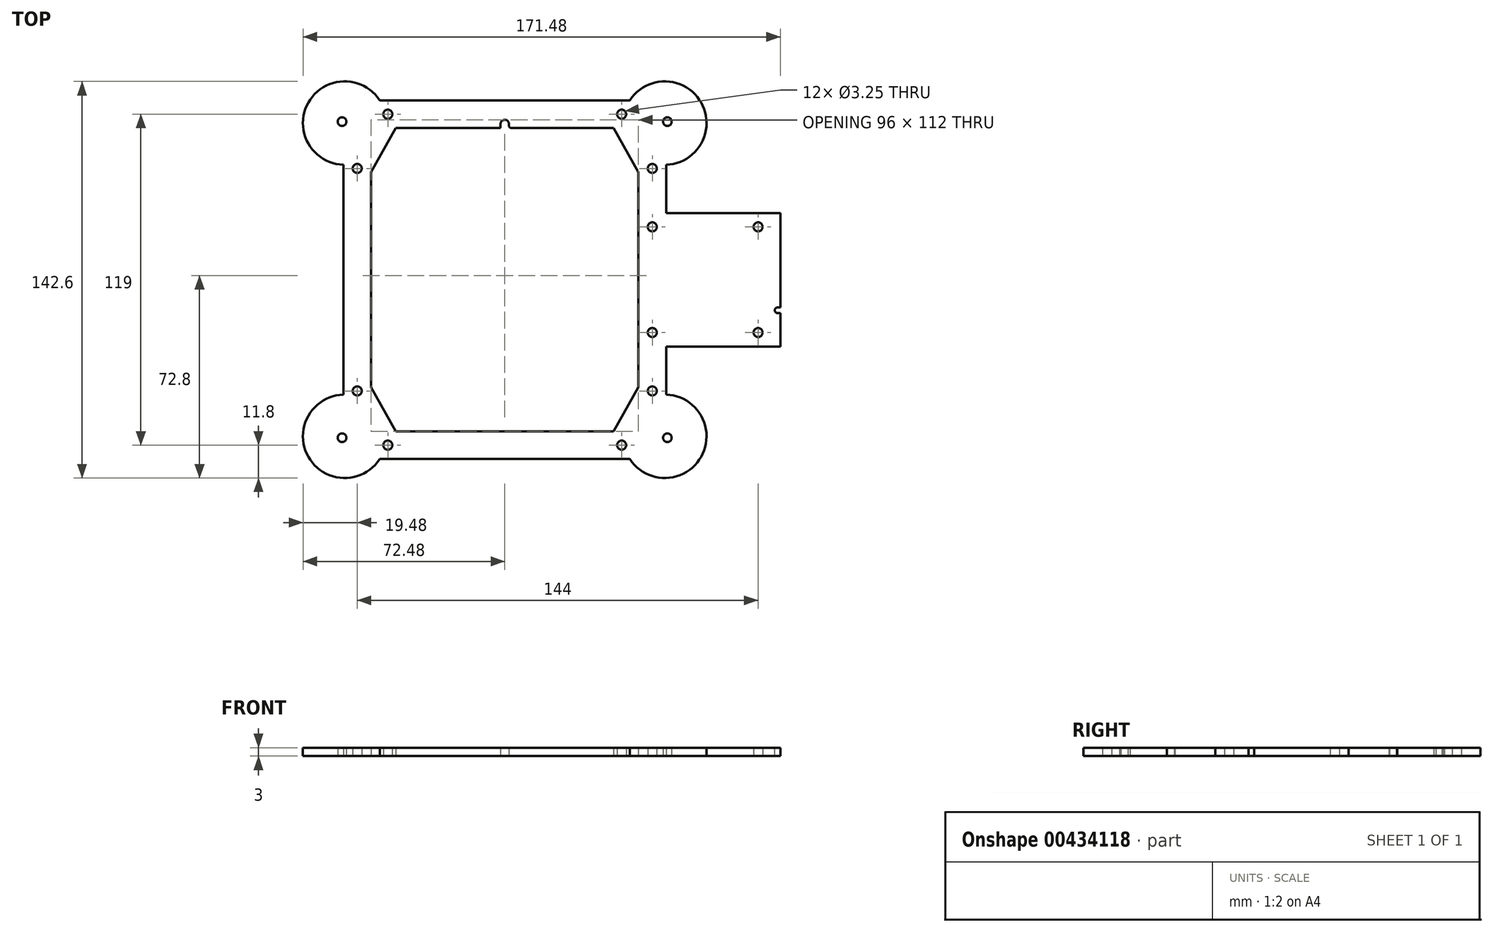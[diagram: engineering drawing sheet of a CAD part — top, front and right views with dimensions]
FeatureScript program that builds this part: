
annotation { "Feature Type Name" : "Feature", "Feature Type Description" : "" }
export const myFeature = defineFeature(function(context is Context, id is Id, definition is map)
    precondition{}
    {
        {
            var Q0;
            Q0=qCreatedBy(makeId("Top.planeOp"),FACE);
            var sketch = newSketch(context, id + "F0", { "sketchPlane" : qUnion([Q0])});
            skLineSegment(sketch, "E0", {"start": v(0, 0) * mm, "end": v(74.97, 0) * mm, "construction": true});
            skLineSegment(sketch, "E1", {"start": v(0, 0) * mm, "end": v(0, 75.03) * mm, "construction": true});
            skCircle(sketch, "E2", {"center": v(53, 40) * mm, "radius": 1.63 * mm});
            skCircle(sketch, "E3.MirrorC", {"center": v(-53, 40) * mm, "radius": 1.63 * mm});
            skCircle(sketch, "E4.MirrorC", {"center": v(-53, -40) * mm, "radius": 1.63 * mm});
            skCircle(sketch, "E5.MirrorC", {"center": v(53, -40) * mm, "radius": 1.63 * mm});
            skCircle(sketch, "E6", {"center": v(42, 59.5) * mm, "radius": 1.63 * mm});
            skCircle(sketch, "E7.MirrorC", {"center": v(-42, 59.5) * mm, "radius": 1.63 * mm});
            skCircle(sketch, "E8.MirrorC", {"center": v(-42, -59.5) * mm, "radius": 1.63 * mm});
            skCircle(sketch, "E9.MirrorC", {"center": v(42, -59.5) * mm, "radius": 1.63 * mm});
            skLineSegment(sketch, "E10", {"start": v(0, 59.5) * mm, "end": v(42, 59.5) * mm, "construction": true});
            skLineSegment(sketch, "E11", {"start": v(42, 59.5) * mm, "end": v(53, 40) * mm, "construction": true});
            skLineSegment(sketch, "E12", {"start": v(53, 40) * mm, "end": v(53, 0) * mm, "construction": true});
            skLineSegment(sketch, "E13.0", {"start": v(48, 38.69) * mm, "end": v(48, 0) * mm});
            skLineSegment(sketch, "E13.1", {"start": v(39.08, 54.5) * mm, "end": v(48, 38.69) * mm});
            skLineSegment(sketch, "E13.2", {"start": v(0, 54.5) * mm, "end": v(39.08, 54.5) * mm});
            skLineSegment(sketch, "E14.0", {"start": v(58, 41.31) * mm, "end": v(58, 24) * mm});
            skLineSegment(sketch, "E14.2", {"start": v(0, 64.5) * mm, "end": v(44.92, 64.5) * mm});
            skLineSegment(sketch, "E15.MirrorCS", {"start": v(-58, 41.31) * mm, "end": v(-58, 0) * mm});
            skLineSegment(sketch, "E16.MirrorCS", {"start": v(-48, 38.69) * mm, "end": v(-48, 0) * mm});
            skLineSegment(sketch, "E17.MirrorCS", {"start": v(-39.08, 54.5) * mm, "end": v(-48, 38.69) * mm});
            skLineSegment(sketch, "E18.MirrorCS", {"start": v(0, 54.5) * mm, "end": v(-39.08, 54.5) * mm});
            skLineSegment(sketch, "E19.MirrorCS", {"start": v(0, 64.5) * mm, "end": v(-44.92, 64.5) * mm});
            skLineSegment(sketch, "E20.MirrorCS", {"start": v(-48, -38.69) * mm, "end": v(-48, 0) * mm});
            skLineSegment(sketch, "E21.MirrorCS", {"start": v(-39.08, -54.5) * mm, "end": v(-48, -38.69) * mm});
            skLineSegment(sketch, "E22.MirrorCS", {"start": v(0, -54.5) * mm, "end": v(-39.08, -54.5) * mm});
            skLineSegment(sketch, "E23.MirrorCS", {"start": v(0, -54.5) * mm, "end": v(39.08, -54.5) * mm});
            skLineSegment(sketch, "E24.MirrorCS", {"start": v(39.08, -54.5) * mm, "end": v(48, -38.69) * mm});
            skLineSegment(sketch, "E25.MirrorCS", {"start": v(48, -38.69) * mm, "end": v(48, 0) * mm});
            skLineSegment(sketch, "E26.MirrorCS", {"start": v(58, -41.31) * mm, "end": v(58, -24) * mm});
            skLineSegment(sketch, "E27.MirrorCS", {"start": v(0, -64.5) * mm, "end": v(44.92, -64.5) * mm});
            skLineSegment(sketch, "E28.MirrorCS", {"start": v(0, -64.5) * mm, "end": v(-44.92, -64.5) * mm});
            skLineSegment(sketch, "E29.MirrorCS", {"start": v(-58, -41.31) * mm, "end": v(-58, 0) * mm});
            skCircle(sketch, "E30.MirrorC", {"center": v(53, 19) * mm, "radius": 1.63 * mm});
            skCircle(sketch, "E31.MirrorC", {"center": v(91, 19) * mm, "radius": 1.63 * mm});
            skLineSegment(sketch, "E32", {"start": v(53, 19) * mm, "end": v(91, 19) * mm, "construction": true});
            skCircle(sketch, "E33.MirrorC", {"center": v(91, -19) * mm, "radius": 1.63 * mm});
            skCircle(sketch, "E34.MirrorC", {"center": v(53, -19) * mm, "radius": 1.63 * mm});
            skLineSegment(sketch, "E35", {"start": v(91, 19) * mm, "end": v(91, -19) * mm, "construction": true});
            skLineSegment(sketch, "E36", {"start": v(91, -19) * mm, "end": v(53, -19) * mm, "construction": true});
            skLineSegment(sketch, "E37.0", {"start": v(86, -14) * mm, "end": v(58, -14) * mm});
            skLineSegment(sketch, "E37.1", {"start": v(86, 14) * mm, "end": v(86, -14) * mm});
            skLineSegment(sketch, "E37.2", {"start": v(58, 14) * mm, "end": v(86, 14) * mm});
            skLineSegment(sketch, "E38.0", {"start": v(99, -24) * mm, "end": v(58, -24) * mm});
            skLineSegment(sketch, "E38.1", {"start": v(99, 24) * mm, "end": v(99, -24) * mm});
            skLineSegment(sketch, "E38.2", {"start": v(58, 24) * mm, "end": v(99, 24) * mm});
            skLineSegment(sketch, "E39.trimOffspring", {"start": v(58, 14) * mm, "end": v(58, 0) * mm});
            skLineSegment(sketch, "E40.trimOffspring", {"start": v(58, -14) * mm, "end": v(58, 0) * mm});
            skPoint(sketch, "E41.center.orphan", {"position": v(51.46, 52.9) * mm});
            skLineSegment(sketch, "E42", {"start": v(44.92, 64.5) * mm, "end": v(58, 41.31) * mm, "construction": true});
            skArc(sketch, "E43.trimOffspring", {"start": v(58, 41.31) * mm, "mid": v(70.55, 63.67) * mm, "end": v(44.92, 64.5) * mm});
            skLineSegment(sketch, "E44", {"start": v(51.46, 52.9) * mm, "end": v(58.43, 56.84) * mm, "construction": true});
            skCircle(sketch, "E45", {"center": v(58.43, 56.84) * mm, "radius": 1.55 * mm});
            skArc(sketch, "E46.MirrorCS", {"start": v(-58, 41.31) * mm, "mid": v(-70.55, 63.67) * mm, "end": v(-44.92, 64.5) * mm});
            skCircle(sketch, "E47.MirrorC", {"center": v(-58.43, 56.84) * mm, "radius": 1.55 * mm});
            skArc(sketch, "E48.MirrorCS", {"start": v(58, -41.31) * mm, "mid": v(70.55, -63.67) * mm, "end": v(44.92, -64.5) * mm});
            skCircle(sketch, "E49.MirrorC", {"center": v(58.43, -56.84) * mm, "radius": 1.55 * mm});
            skCircle(sketch, "E50.MirrorC", {"center": v(-58.43, -56.84) * mm, "radius": 1.55 * mm});
            skArc(sketch, "E51.MirrorCS", {"start": v(-58, -41.31) * mm, "mid": v(-70.55, -63.67) * mm, "end": v(-44.92, -64.5) * mm});
            skSolve(sketch);
        }
        {
            var Q0;
            Q0 = qSketchRegion(id + "F0", true);
            extrude(context, id + "F1", {"entities" : qUnion([Q0]), "depth" : 3 * mm});
        }
        {
            var Q0;
            Q0=qCreatedBy(makeId("Top.planeOp"),FACE);
            var sketch = newSketch(context, id + "F2", { "sketchPlane" : qUnion([Q0])});
            skLineSegment(sketch, "E52.bottom", {"start": v(57.9, 14.1) * mm, "end": v(86.1, 14.1) * mm});
            skLineSegment(sketch, "E52.top", {"start": v(57.9, -14.1) * mm, "end": v(86.1, -14.1) * mm});
            skLineSegment(sketch, "E52.left", {"start": v(57.9, 14.1) * mm, "end": v(57.9, -14.1) * mm});
            skLineSegment(sketch, "E52.right", {"start": v(86.1, 14.1) * mm, "end": v(86.1, -14.1) * mm});
            skSolve(sketch);
        }
        {
            var Q0;
            Q0 = qSketchRegion(id + "F2", true);
            extrude(context, id + "F3", {"entities" : qUnion([Q0]), "operationType" : NewBodyOperationType.ADD, "depth" : 3 * mm});
        }
        {
            var Q0;
            Q0=makeQuery(id+"F3.boolean.opBoolean","MERGE",FACE,{"derivedFrom":[makeQuery(id+"F1.opExtrude","CAP_FACE",FACE,{"disambiguationData":[OSD([sQuery(id+"F0.wireOp",EDGE,"E2"),sQuery(id+"F0.wireOp",EDGE,"E3.MirrorC"),sQuery(id+"F0.wireOp",EDGE,"E4.MirrorC"),sQuery(id+"F0.wireOp",EDGE,"E5.MirrorC"),sQuery(id+"F0.wireOp",EDGE,"E6"),sQuery(id+"F0.wireOp",EDGE,"E7.MirrorC"),sQuery(id+"F0.wireOp",EDGE,"E8.MirrorC"),sQuery(id+"F0.wireOp",EDGE,"E9.MirrorC"),sQuery(id+"F0.wireOp",EDGE,"E13.0"),sQuery(id+"F0.wireOp",EDGE,"E13.1"),sQuery(id+"F0.wireOp",EDGE,"E13.2"),sQuery(id+"F0.wireOp",EDGE,"E14.0"),sQuery(id+"F0.wireOp",EDGE,"E14.2"),sQuery(id+"F0.wireOp",EDGE,"E15.MirrorCS"),sQuery(id+"F0.wireOp",EDGE,"E16.MirrorCS"),sQuery(id+"F0.wireOp",EDGE,"E17.MirrorCS"),sQuery(id+"F0.wireOp",EDGE,"E18.MirrorCS"),sQuery(id+"F0.wireOp",EDGE,"E19.MirrorCS"),sQuery(id+"F0.wireOp",EDGE,"E20.MirrorCS"),sQuery(id+"F0.wireOp",EDGE,"E21.MirrorCS"),sQuery(id+"F0.wireOp",EDGE,"E22.MirrorCS"),sQuery(id+"F0.wireOp",EDGE,"E23.MirrorCS"),sQuery(id+"F0.wireOp",EDGE,"E24.MirrorCS"),sQuery(id+"F0.wireOp",EDGE,"E25.MirrorCS"),sQuery(id+"F0.wireOp",EDGE,"E26.MirrorCS"),sQuery(id+"F0.wireOp",EDGE,"E27.MirrorCS"),sQuery(id+"F0.wireOp",EDGE,"E28.MirrorCS"),sQuery(id+"F0.wireOp",EDGE,"E29.MirrorCS"),sQuery(id+"F0.wireOp",EDGE,"E30.MirrorC"),sQuery(id+"F0.wireOp",EDGE,"E31.MirrorC"),sQuery(id+"F0.wireOp",EDGE,"E33.MirrorC"),sQuery(id+"F0.wireOp",EDGE,"E34.MirrorC"),sQuery(id+"F0.wireOp",EDGE,"E37.0"),sQuery(id+"F0.wireOp",EDGE,"E37.1"),sQuery(id+"F0.wireOp",EDGE,"E37.2"),sQuery(id+"F0.wireOp",EDGE,"E38.0"),sQuery(id+"F0.wireOp",EDGE,"E38.1"),sQuery(id+"F0.wireOp",EDGE,"E38.2"),sQuery(id+"F0.wireOp",EDGE,"E39.trimOffspring"),sQuery(id+"F0.wireOp",EDGE,"E40.trimOffspring"),sQuery(id+"F0.wireOp",EDGE,"E43.trimOffspring"),sQuery(id+"F0.wireOp",EDGE,"E45"),sQuery(id+"F0.wireOp",EDGE,"E46.MirrorCS"),sQuery(id+"F0.wireOp",EDGE,"E47.MirrorC"),sQuery(id+"F0.wireOp",EDGE,"E48.MirrorCS"),sQuery(id+"F0.wireOp",EDGE,"E49.MirrorC"),sQuery(id+"F0.wireOp",EDGE,"E50.MirrorC"),sQuery(id+"F0.wireOp",EDGE,"E51.MirrorCS")])],"isStart":false}),makeQuery(id+"F3.opExtrude","CAP_FACE",FACE,{"disambiguationData":[OSD([sQuery(id+"F2.wireOp",EDGE,"E52.bottom"),sQuery(id+"F2.wireOp",EDGE,"E52.top"),sQuery(id+"F2.wireOp",EDGE,"E52.left"),sQuery(id+"F2.wireOp",EDGE,"E52.right")])],"isStart":false})]});
            var sketch = newSketch(context, id + "F4", { "sketchPlane" : qUnion([Q0])});
            skArc(sketch, "E53", {"start": v(98, -10) * mm, "mid": v(97, -11) * mm, "end": v(98, -12) * mm});
            skLineSegment(sketch, "E54", {"start": v(98, -10) * mm, "end": v(99, -10) * mm});
            skLineSegment(sketch, "E55", {"start": v(98, -12) * mm, "end": v(99, -12) * mm});
            skLineSegment(sketch, "E56", {"start": v(99, -10) * mm, "end": v(99, -12) * mm});
            skSolve(sketch);
        }
        {
            var Q0;
            Q0 = qSketchRegion(id + "F4", true);
            extrude(context, id + "F5", {"entities" : qUnion([Q0]), "operationType" : NewBodyOperationType.REMOVE, "oppositeDirection" : true, "depth" : 25 * mm});
        }
        {
            var Q0;
            Q0=qCreatedBy(makeId("Top.planeOp"),FACE);
            var sketch = newSketch(context, id + "F6", { "sketchPlane" : qUnion([Q0])});
            skArc(sketch, "E57", {"start": v(1.5, 56) * mm, "mid": v(0, 57.5) * mm, "end": v(-1.5, 56) * mm});
            skLineSegment(sketch, "E58", {"start": v(-1.5, 56) * mm, "end": v(-1.5, 54.5) * mm});
            skLineSegment(sketch, "E59", {"start": v(1.5, 56) * mm, "end": v(1.5, 54.5) * mm});
            skLineSegment(sketch, "E60", {"start": v(1.5, 54.5) * mm, "end": v(-1.5, 54.5) * mm});
            skSolve(sketch);
        }
        {
            var Q0;
            Q0 = qSketchRegion(id + "F6", true);
            extrude(context, id + "F7", {"entities" : qUnion([Q0]), "operationType" : NewBodyOperationType.REMOVE, "depth" : 25 * mm});
        }
        {
            var Q0;
            Q0=makeQuery(id+"F7.boolean.opBoolean","COPY",EDGE,{"derivedFrom":makeQuery(id+"F7.opExtrude","SWEPT_EDGE",EDGE,{"disambiguationData":[OSD([sQuery(id+"F6.wireOp",EDGE,"E58"),sQuery(id+"F6.wireOp",EDGE,"E60")])]})});
            var Q1;
            Q1=makeQuery(id+"F7.boolean.opBoolean","COPY",EDGE,{"derivedFrom":makeQuery(id+"F7.opExtrude","SWEPT_EDGE",EDGE,{"disambiguationData":[OSD([sQuery(id+"F6.wireOp",EDGE,"E59"),sQuery(id+"F6.wireOp",EDGE,"E60")])]})});
            fillet(context, id + "F8", {"entities" : qUnion([Q0, Q1]), "radius" : 1 * mm, "tangentPropagation" : true, "allowEdgeOverflow" : false});
        }
    });
